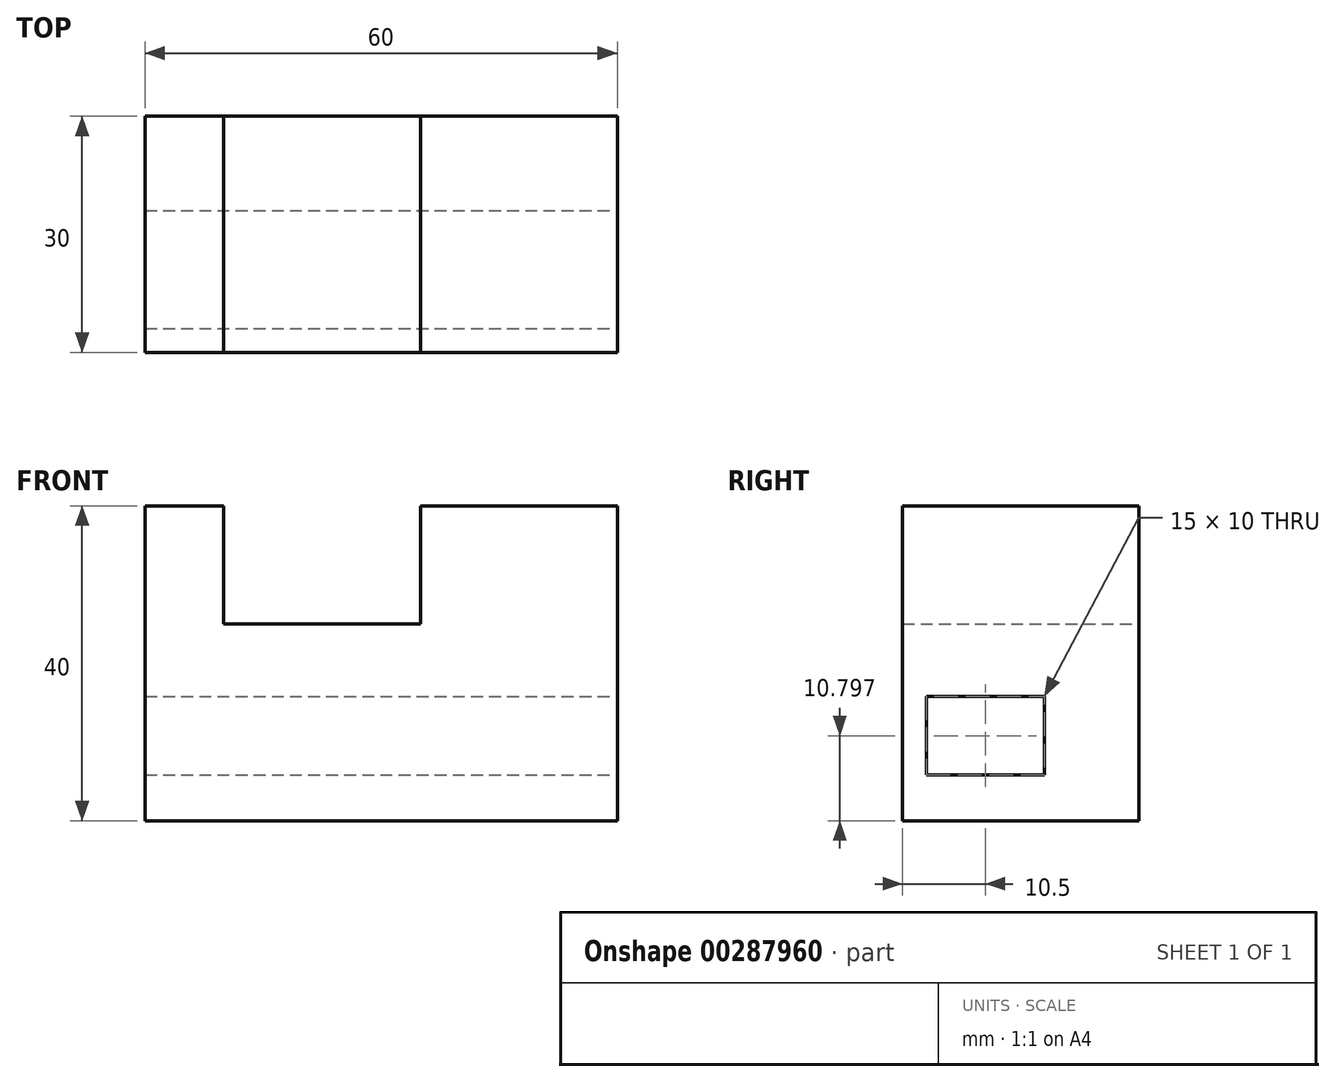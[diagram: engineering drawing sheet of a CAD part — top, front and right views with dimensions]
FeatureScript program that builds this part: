
annotation { "Feature Type Name" : "Feature", "Feature Type Description" : "" }
export const myFeature = defineFeature(function(context is Context, id is Id, definition is map)
    precondition{}
    {
        {
            var Q0;
            Q0=qCreatedBy(makeId("Front.planeOp"),FACE);
            var sketch = newSketch(context, id + "F0", { "sketchPlane" : qUnion([Q0])});
            skLineSegment(sketch, "E0.bottom", {"start": v(-16.98, 1.96) * mm, "end": v(43.02, 1.96) * mm});
            skLineSegment(sketch, "E0.top", {"start": v(-16.98, -38.04) * mm, "end": v(43.02, -38.04) * mm});
            skLineSegment(sketch, "E0.left", {"start": v(-16.98, 1.96) * mm, "end": v(-16.98, -38.04) * mm});
            skLineSegment(sketch, "E0.right", {"start": v(43.02, 1.96) * mm, "end": v(43.02, -38.04) * mm});
            skLineSegment(sketch, "E1.bottom", {"start": v(-6.98, 1.96) * mm, "end": v(18.02, 1.96) * mm});
            skLineSegment(sketch, "E1.top", {"start": v(-6.98, -13.04) * mm, "end": v(18.02, -13.04) * mm});
            skLineSegment(sketch, "E1.left", {"start": v(-6.98, 1.96) * mm, "end": v(-6.98, -13.04) * mm});
            skLineSegment(sketch, "E1.right", {"start": v(18.02, 1.96) * mm, "end": v(18.02, -13.04) * mm});
            skSolve(sketch);
        }
        {
            var Q0;
            Q0=makeQuery(id+"F0.imprint","IMPRINT",FACE,{"disambiguationData":[TD([[makeQuery(id+"F0.imprint","IMPRINT",EDGE,{"derivedFrom":sQuery(id+"F0.wireOp",EDGE,"E0.top")}),1.0]])]});
            extrude(context, id + "F1", {"entities" : qUnion([Q0]), "depth" : 30 * mm});
        }
        {
            var Q0;
            Q0=makeQuery(id+"F1.opExtrude","SWEPT_FACE",FACE,{"disambiguationData":[OSD([sQuery(id+"F0.wireOp",EDGE,"E0.right")])]});
            var sketch = newSketch(context, id + "F2", { "sketchPlane" : qUnion([Q0])});
            skLineSegment(sketch, "E2.bottom", {"start": v(-27, -22.24) * mm, "end": v(-12, -22.24) * mm});
            skLineSegment(sketch, "E2.top", {"start": v(-27, -32.24) * mm, "end": v(-12, -32.24) * mm});
            skLineSegment(sketch, "E2.left", {"start": v(-27, -22.24) * mm, "end": v(-27, -32.24) * mm});
            skLineSegment(sketch, "E2.right", {"start": v(-12, -22.24) * mm, "end": v(-12, -32.24) * mm});
            skSolve(sketch);
        }
        {
            var Q0;
            Q0=makeQuery(id+"F2.imprint","IMPRINT",FACE,{"disambiguationData":[TD([[makeQuery(id+"F2.imprint","IMPRINT",EDGE,{"derivedFrom":sQuery(id+"F2.wireOp",EDGE,"E2.bottom")}),-1.0]])]});
            extrude(context, id + "F3", {"entities" : qUnion([Q0]), "operationType" : NewBodyOperationType.REMOVE, "oppositeDirection" : true, "depth" : 127 * mm});
        }
    });
